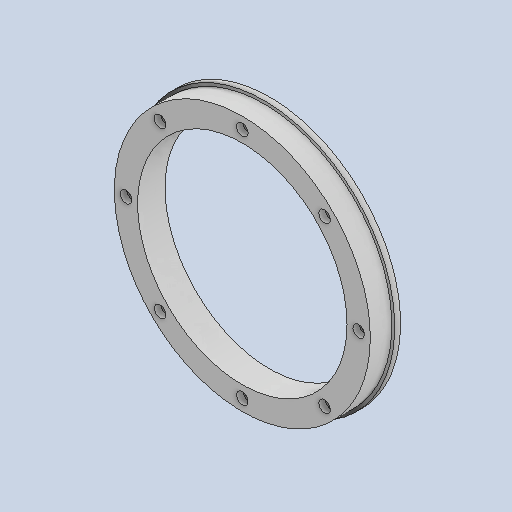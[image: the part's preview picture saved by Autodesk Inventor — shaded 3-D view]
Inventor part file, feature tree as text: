
AUTODESK INVENTOR PART (.ipt)
format: ipt  version: 2024.2 (Build 282272000, 272)  size: 163,328 bytes
history: native  units: mm
features: extrude x4, sketch x4, pattern_circular x1, projected_geometry x1
ambient origin geometry x8: Origin, YZ Plane, XZ Plane, XY Plane, X Axis, Y Axis, Z Axis, Center Point
bodies: Solid1 (feature_tree)
feature tree (10):
  extrude  "Extrusion1"  Depth=360.0mm
  extrude  "Extrusion2"  Depth=47.0mm
  extrude  "Extrusion3"  Depth=80.0mm TaperAngle=360.0deg
  pattern_circular  "Circular Pattern1"  Count=2  [1 undecoded]
  extrude  "Extrusion4"  Depth=10.0mm
  sketch  "Sketch1"  dims[d0=40.0mm d1=360.0mm]
  sketch  "Sketch2"  dims[d2=47.0mm d3=0.0mm d4=12.5mm]
  projected_geometry  "Projected Loop1"
  sketch  "Sketch3"  dims[d5=0.0mm d6=0.0mm d7=80.0mm d8=360.0deg d10=20.0mm]
  sketch  "Sketch4"  dims[d11=11.0mm d12=0.0mm d13=5.0mm d14=10.0mm d15=0.0mm]
note: 1 required parameter value undecoded (feature->parameter linkage not recoverable at this tier; creation-order binding heuristic only, values carry confidence <= 0.55)
